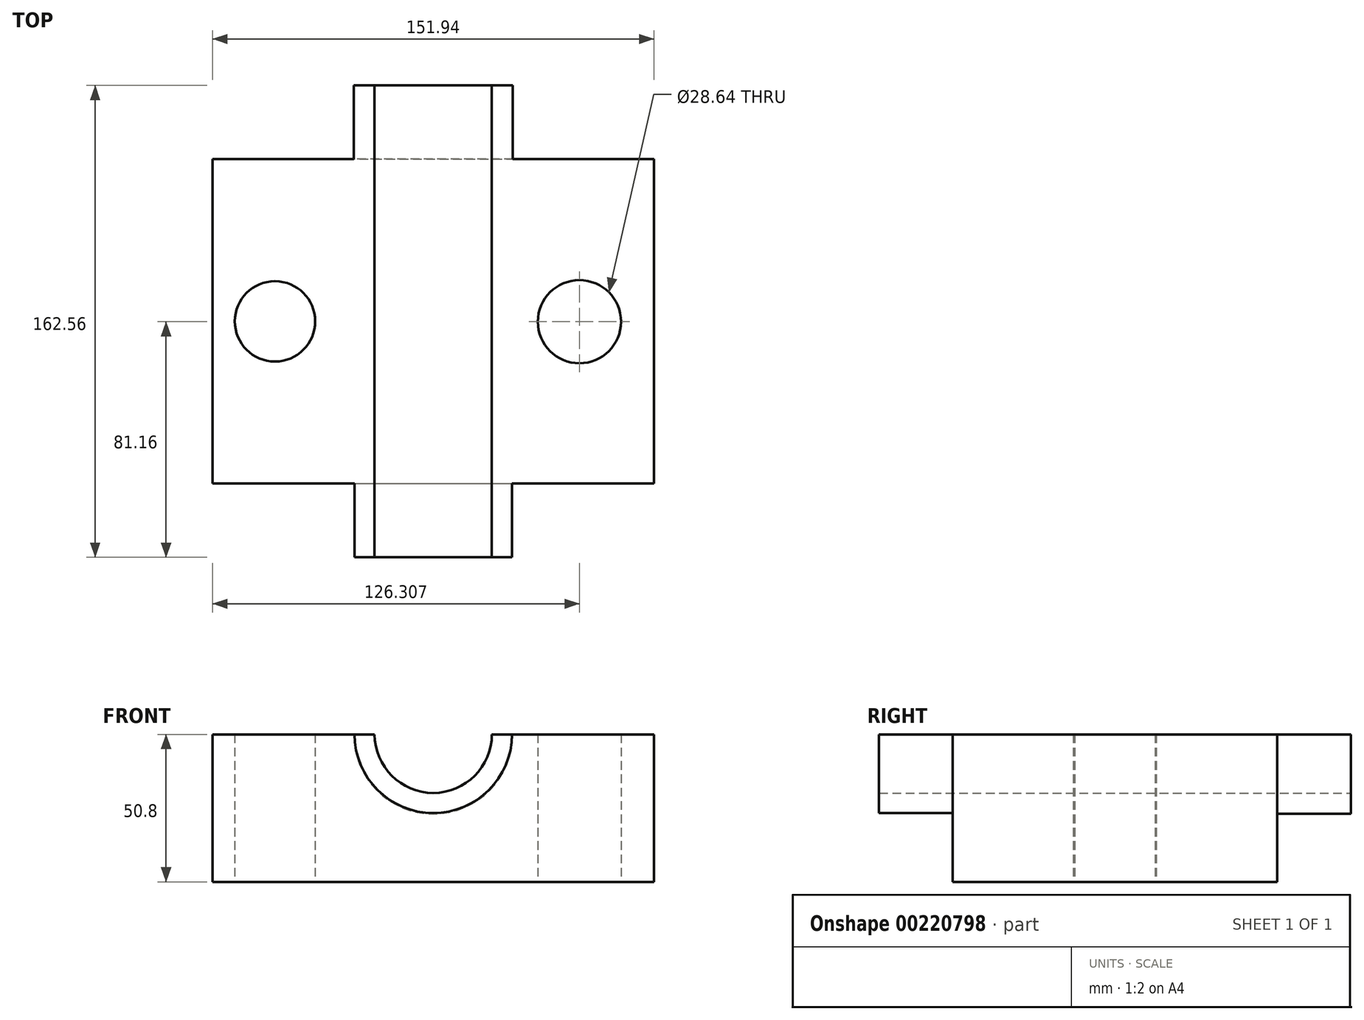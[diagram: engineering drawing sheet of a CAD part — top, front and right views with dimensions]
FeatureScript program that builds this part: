
annotation { "Feature Type Name" : "Feature", "Feature Type Description" : "" }
export const myFeature = defineFeature(function(context is Context, id is Id, definition is map)
    precondition{}
    {
        {
            var Q0;
            Q0=qCreatedBy(makeId("Top.planeOp"),FACE);
            var sketch = newSketch(context, id + "F0", { "sketchPlane" : qUnion([Q0])});
            skLineSegment(sketch, "E0.bottom", {"start": v(-76.2, 56) * mm, "end": v(75.74, 56) * mm});
            skLineSegment(sketch, "E0.top", {"start": v(-76.2, -55.76) * mm, "end": v(75.74, -55.76) * mm});
            skLineSegment(sketch, "E0.left", {"start": v(-76.2, 56) * mm, "end": v(-76.2, -55.76) * mm});
            skLineSegment(sketch, "E0.right", {"start": v(75.74, 56) * mm, "end": v(75.74, -55.76) * mm});
            skCircle(sketch, "E1", {"center": v(-54.73, 0.12) * mm, "radius": 13.83 * mm});
            skPoint(sketch, "E1.centerSnap0", {"position": v(-76.2, 0.12) * mm});
            skCircle(sketch, "E2", {"center": v(50.1, 0) * mm, "radius": 14.32 * mm});
            skSolve(sketch);
        }
        {
            var Q0;
            Q0=makeQuery(id+"F0.imprint","IMPRINT",FACE,{"disambiguationData":[TD([[makeQuery(id+"F0.imprint","IMPRINT",EDGE,{"derivedFrom":sQuery(id+"F0.wireOp",EDGE,"E0.bottom")}),-1.0]])]});
            extrude(context, id + "F1", {"entities" : qUnion([Q0]), "depth" : 50.8 * mm});
        }
        {
            var Q0;
            Q0=makeQuery(id+"F1.opExtrude","SWEPT_FACE",FACE,{"disambiguationData":[OSD([sQuery(id+"F0.wireOp",EDGE,"E0.top")])]});
            var sketch = newSketch(context, id + "F2", { "sketchPlane" : qUnion([Q0])});
            skCircle(sketch, "E3", {"center": v(-0.23, 50.8) * mm, "radius": 27.1 * mm});
            skCircle(sketch, "E4", {"center": v(-0.23, 50.8) * mm, "radius": 20.2 * mm});
            skSolve(sketch);
        }
        {
            var Q0;
            {var subQ0=sQuery(id+"F2.wireOp",EDGE,"E3");var subQ1=makeQuery(id+"F1.opExtrude","CAP_EDGE",EDGE,{"disambiguationData":[OSD([sQuery(id+"F0.wireOp",EDGE,"E0.top")])],"isStart":false});var subQ2=makeQuery(id+"F2.imprint","INTERSECT",VERTEX,{"disambiguationData":[OD(0.0)],"derivedFrom":[subQ1,subQ0]});Q0=makeQuery(id+"F2.imprint","IMPRINT",FACE,{"disambiguationData":[TD([[makeQuery(id+"F2.imprint","IMPRINT",EDGE,{"disambiguationData":[TD([[subQ2,-1.0]])],"derivedFrom":subQ0}),1.0]])]});}
            extrude(context, id + "F3", {"entities" : qUnion([Q0]), "operationType" : NewBodyOperationType.ADD, "depth" : 25.4 * mm});
        }
        {
            var Q0;
            {var subQ0=sQuery(id+"F0.wireOp",EDGE,"E0.top");var subQ1=sQuery(id+"F2.wireOp",EDGE,"E4");Q0=makeQuery(id+"F3.boolean.opBoolean","SPLIT",FACE,{"disambiguationData":[TD([makeQuery(id+"F3.opExtrude","SWEPT_FACE",FACE,{"disambiguationData":[OSD([subQ1])]})])],"derivedFrom":makeQuery(id+"F1.opExtrude","SWEPT_FACE",FACE,{"disambiguationData":[OSD([subQ0])]})});}
            extrude(context, id + "F4", {"entities" : qUnion([Q0]), "operationType" : NewBodyOperationType.REMOVE, "oppositeDirection" : true, "depth" : 127 * mm});
        }
        {
            var Q0;
            Q0=makeQuery(id+"F1.opExtrude","SWEPT_FACE",FACE,{"disambiguationData":[OSD([sQuery(id+"F0.wireOp",EDGE,"E0.bottom")])]});
            var sketch = newSketch(context, id + "F5", { "sketchPlane" : qUnion([Q0])});
            skCircle(sketch, "E5", {"center": v(0.23, 50.8) * mm, "radius": 27.4 * mm});
            skSolve(sketch);
        }
        {
            var Q0;
            {var subQ2=sQuery(id+"F2.wireOp",EDGE,"E4");var subQ3=makeQuery(id+"F4.opExtrude","SWEPT_FACE",FACE,{"disambiguationData":[OSD([subQ2])]});var subQ6=sQuery(id+"F0.wireOp",EDGE,"E0.bottom");var subQ9=makeQuery(id+"F1.opExtrude","SWEPT_FACE",FACE,{"disambiguationData":[OSD([subQ6])]});var subQ19=makeQuery(id+"F4.boolean.opBoolean","INTERSECT",EDGE,{"derivedFrom":[subQ9,subQ3]});Q0=makeQuery(id+"F5.imprint","IMPRINT",FACE,{"disambiguationData":[TD([[makeQuery(id+"F5.imprint","IMPRINT",EDGE,{"derivedFrom":subQ19}),-1.0]])]});}
            extrude(context, id + "F6", {"entities" : qUnion([Q0]), "operationType" : NewBodyOperationType.ADD, "depth" : 25.4 * mm});
        }
    });
